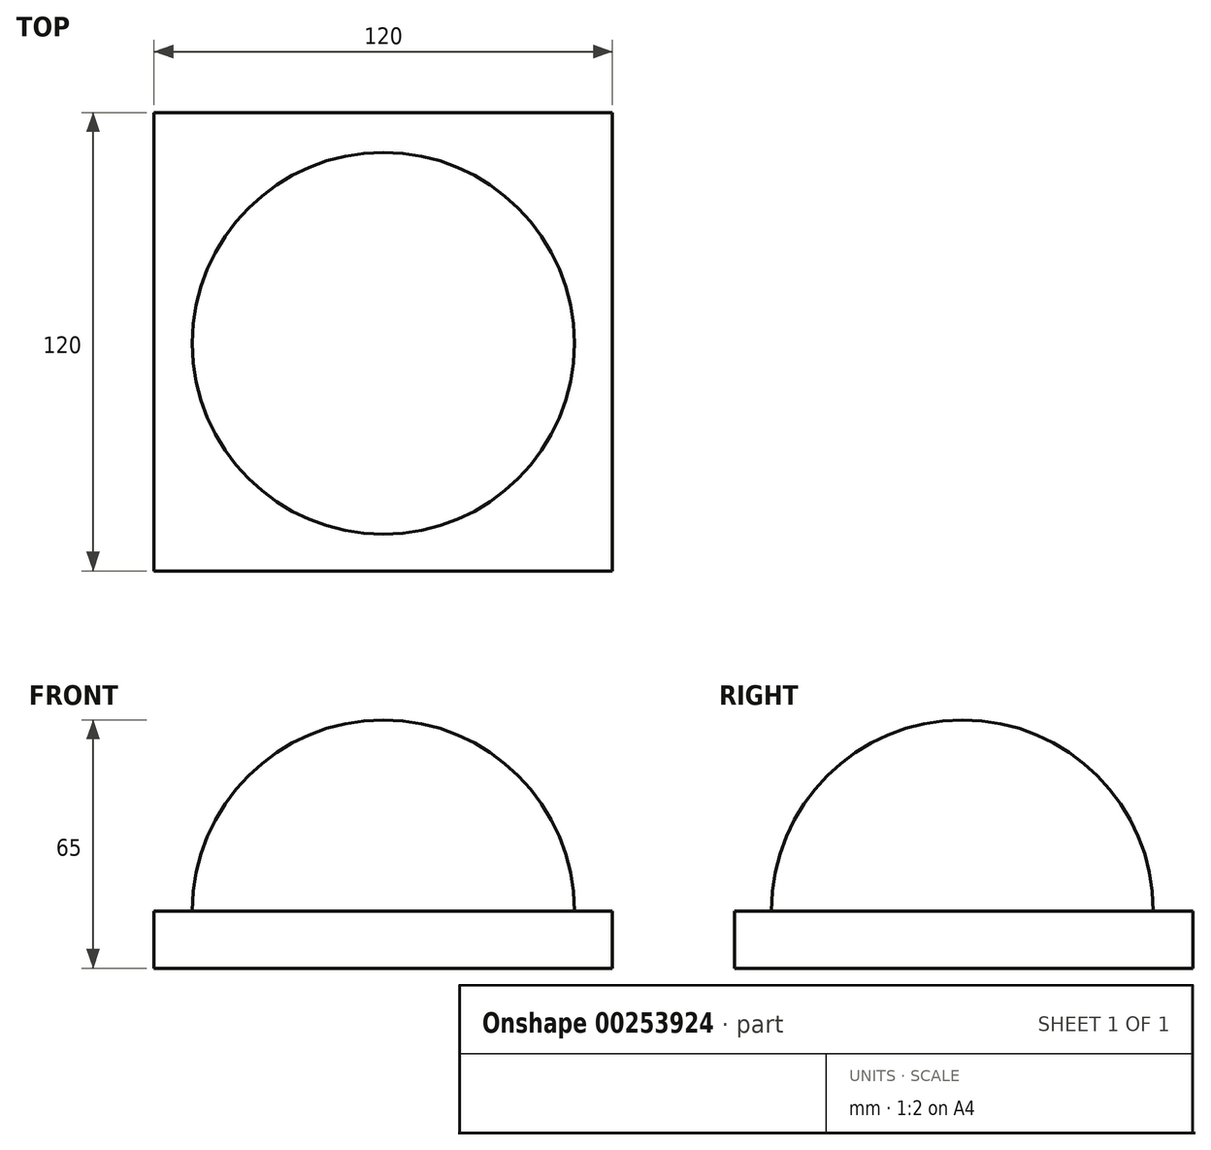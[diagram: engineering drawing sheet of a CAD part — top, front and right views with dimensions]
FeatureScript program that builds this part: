
annotation { "Feature Type Name" : "Feature", "Feature Type Description" : "" }
export const myFeature = defineFeature(function(context is Context, id is Id, definition is map)
    precondition{}
    {
        {
            var Q0;
            Q0=qCreatedBy(makeId("Top.planeOp"),FACE);
            var sketch = newSketch(context, id + "F0", { "sketchPlane" : qUnion([Q0])});
            skLineSegment(sketch, "E0.bottom", {"start": v(60, -60) * mm, "end": v(-60, -60) * mm});
            skLineSegment(sketch, "E0.top", {"start": v(60, 60) * mm, "end": v(-60, 60) * mm});
            skLineSegment(sketch, "E0.left", {"start": v(60, -60) * mm, "end": v(60, 60) * mm});
            skLineSegment(sketch, "E0.right", {"start": v(-60, -60) * mm, "end": v(-60, 60) * mm});
            skPoint(sketch, "E0.middle", {"position": v(0, 0) * mm});
            skSolve(sketch);
        }
        {
            var Q0;
            Q0=makeQuery(id+"F0.imprint","IMPRINT",FACE,{"disambiguationData":[TD([[makeQuery(id+"F0.imprint","IMPRINT",EDGE,{"derivedFrom":sQuery(id+"F0.wireOp",EDGE,"E0.bottom")}),-1.0]])]});
            extrude(context, id + "F1", {"entities" : qUnion([Q0]), "depth" : 15 * mm});
        }
        {
            var Q0;
            Q0=makeQuery(id+"F1.opExtrude","CAP_FACE",FACE,{"disambiguationData":[OSD([sQuery(id+"F0.wireOp",EDGE,"E0.bottom"),sQuery(id+"F0.wireOp",EDGE,"E0.top"),sQuery(id+"F0.wireOp",EDGE,"E0.left"),sQuery(id+"F0.wireOp",EDGE,"E0.right")])],"isStart":false});
            var sketch = newSketch(context, id + "F2", { "sketchPlane" : qUnion([Q0])});
            skLineSegment(sketch, "E1", {"start": v(-50, -0.4) * mm, "end": v(50, -0.4) * mm});
            skArc(sketch, "E2", {"start": v(50, -0.4) * mm, "mid": v(0, 49.6) * mm, "end": v(-50, -0.4) * mm});
            skSolve(sketch);
        }
        {
            var Q0;
            Q0=makeQuery(id+"F2.imprint","IMPRINT",FACE,{"disambiguationData":[TD([[makeQuery(id+"F2.imprint","IMPRINT",EDGE,{"derivedFrom":sQuery(id+"F2.wireOp",EDGE,"E1")}),1.0]])]});
            var Q1;
            Q1=sQuery(id+"F2.wireOp",EDGE,"E1");
            revolve(context, id + "F3", {"operationType" : NewBodyOperationType.ADD, "entities" : qUnion([Q0]), "axis" : qUnion([Q1]), "revolveType" : RevolveType.ONE_DIRECTION, "angle" : 180 * degree});
        }
    });
